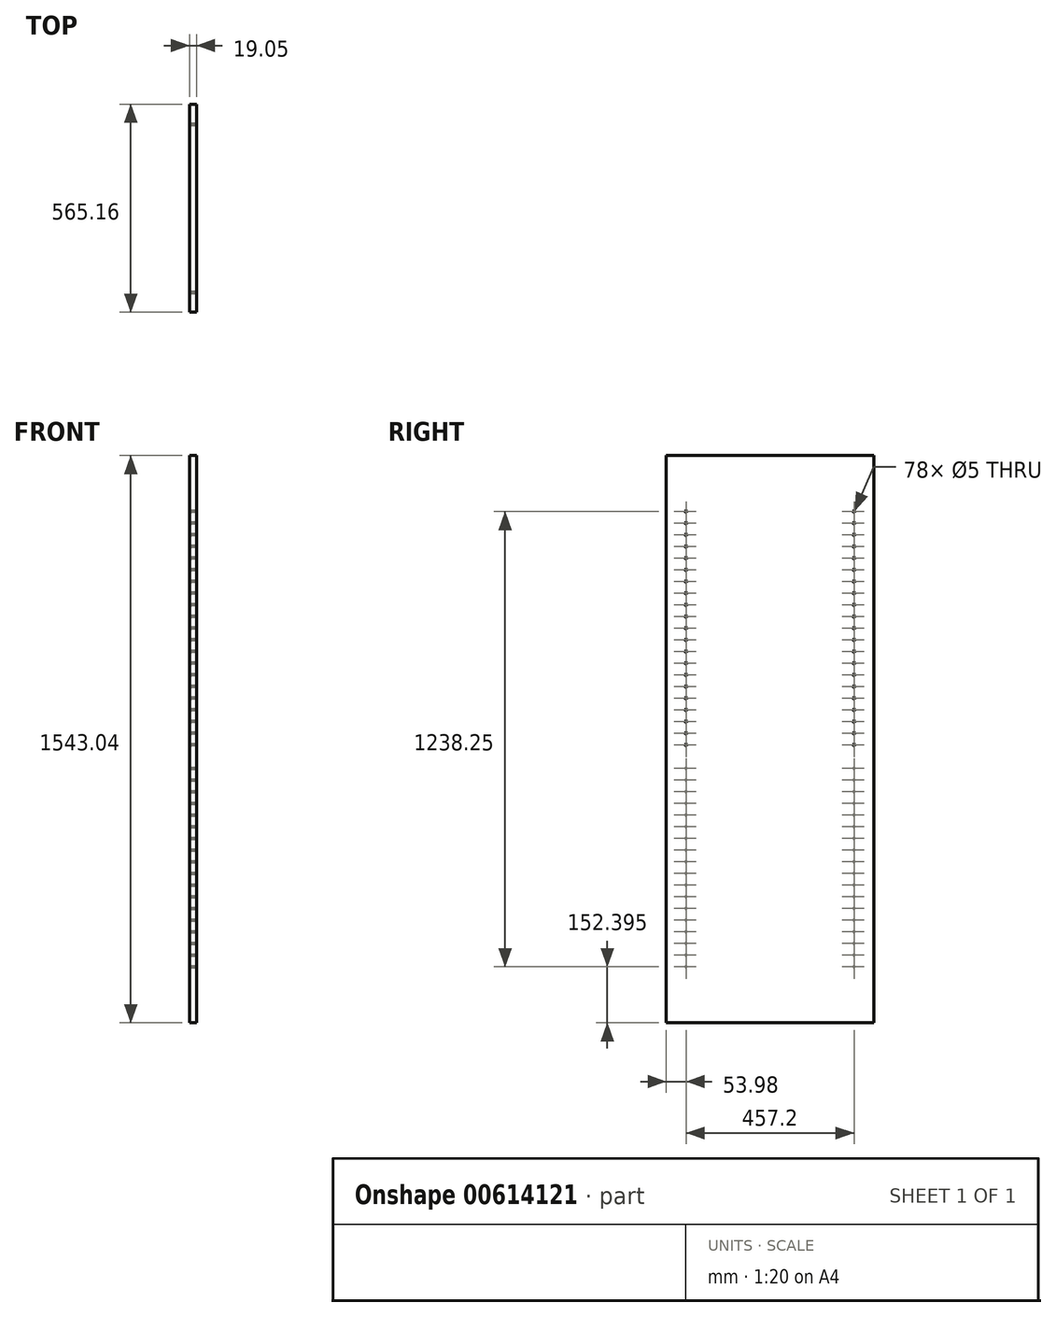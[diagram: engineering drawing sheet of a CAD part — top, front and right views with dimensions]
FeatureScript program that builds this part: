
annotation { "Feature Type Name" : "Feature", "Feature Type Description" : "" }
export const myFeature = defineFeature(function(context is Context, id is Id, definition is map)
    precondition{}
    {
        {
            var Q0;
            Q0=qCreatedBy(makeId("Right.planeOp"),FACE);
            var sketch = newSketch(context, id + "F0", { "sketchPlane" : qUnion([Q0])});
            skLineSegment(sketch, "E0.bottom", {"start": v(282.58, 771.53) * mm, "end": v(-282.57, 771.53) * mm});
            skLineSegment(sketch, "E0.top", {"start": v(282.57, -771.53) * mm, "end": v(-282.58, -771.53) * mm});
            skLineSegment(sketch, "E0.left", {"start": v(282.58, 771.53) * mm, "end": v(282.57, -771.53) * mm});
            skLineSegment(sketch, "E0.right", {"start": v(-282.57, 771.53) * mm, "end": v(-282.58, -771.53) * mm});
            skPoint(sketch, "E0.middle", {"position": v(0, 0) * mm});
            skSolve(sketch);
        }
        {
            var Q0;
            Q0=makeQuery(id+"F0.imprint","IMPRINT",FACE,{"disambiguationData":[TD([[makeQuery(id+"F0.imprint","IMPRINT",EDGE,{"derivedFrom":sQuery(id+"F0.wireOp",EDGE,"E0.bottom")}),1.0]])]});
            extrude(context, id + "F1", {"entities" : qUnion([Q0]), "depth" : 19.05 * mm, "offsetDistance" : 25.4 * mm});
        }
        {
            var Q0;
            Q0=makeQuery(id+"F1.opExtrude","CAP_FACE",FACE,{"disambiguationData":[OSD([sQuery(id+"F0.wireOp",EDGE,"E0.bottom"),sQuery(id+"F0.wireOp",EDGE,"E0.top"),sQuery(id+"F0.wireOp",EDGE,"E0.left"),sQuery(id+"F0.wireOp",EDGE,"E0.right")])],"isStart":false});
            var sketch = newSketch(context, id + "F2", { "sketchPlane" : qUnion([Q0])});
            skLineSegment(sketch, "E1", {"start": v(0, -771.53) * mm, "end": v(0, -9.53) * mm});
            skPoint(sketch, "E1.endSnap0", {"position": v(0, -771.53) * mm});
            skLineSegment(sketch, "E2", {"start": v(0, -9.53) * mm, "end": v(-282.58, -9.53) * mm});
            skLineSegment(sketch, "E3", {"start": v(0, 771.53) * mm, "end": v(0, 587.38) * mm});
            skPoint(sketch, "E3.endSnap0", {"position": v(0, 771.53) * mm});
            skLineSegment(sketch, "E4.bottom", {"start": v(228.6, 555.63) * mm, "end": v(-228.6, 555.63) * mm});
            skLineSegment(sketch, "E4.top", {"start": v(228.6, 619.13) * mm, "end": v(-228.6, 619.13) * mm});
            skLineSegment(sketch, "E4.left", {"start": v(228.6, 555.63) * mm, "end": v(228.6, 619.13) * mm});
            skLineSegment(sketch, "E4.right", {"start": v(-228.6, 555.63) * mm, "end": v(-228.6, 619.13) * mm});
            skPoint(sketch, "E4.middle", {"position": v(0, 587.38) * mm});
            skLineSegment(sketch, "E5", {"start": v(0, 555.63) * mm, "end": v(0, 492.13) * mm});
            skLineSegment(sketch, "E6.bottom", {"start": v(228.6, 523.88) * mm, "end": v(-228.6, 523.88) * mm});
            skLineSegment(sketch, "E6.top", {"start": v(228.6, 460.38) * mm, "end": v(-228.6, 460.38) * mm});
            skLineSegment(sketch, "E6.left", {"start": v(228.6, 523.88) * mm, "end": v(228.6, 460.38) * mm});
            skLineSegment(sketch, "E6.right", {"start": v(-228.6, 523.88) * mm, "end": v(-228.6, 460.38) * mm});
            skPoint(sketch, "E6.middle", {"position": v(0, 492.13) * mm});
            skLineSegment(sketch, "E7", {"start": v(0, 460.38) * mm, "end": v(0, 396.88) * mm});
            skLineSegment(sketch, "E8.bottom", {"start": v(228.6, 365.12) * mm, "end": v(-228.6, 365.12) * mm});
            skLineSegment(sketch, "E8.top", {"start": v(228.6, 428.62) * mm, "end": v(-228.6, 428.62) * mm});
            skLineSegment(sketch, "E8.left", {"start": v(228.6, 365.12) * mm, "end": v(228.6, 428.62) * mm});
            skLineSegment(sketch, "E8.right", {"start": v(-228.6, 365.12) * mm, "end": v(-228.6, 428.62) * mm});
            skPoint(sketch, "E8.middle", {"position": v(0, 396.88) * mm});
            skLineSegment(sketch, "E9", {"start": v(0, 365.12) * mm, "end": v(0, 301.62) * mm});
            skLineSegment(sketch, "E10.bottom", {"start": v(228.6, 333.38) * mm, "end": v(-228.6, 333.38) * mm});
            skLineSegment(sketch, "E10.top", {"start": v(228.6, 269.88) * mm, "end": v(-228.6, 269.87) * mm});
            skLineSegment(sketch, "E10.left", {"start": v(228.6, 333.38) * mm, "end": v(228.6, 269.88) * mm});
            skLineSegment(sketch, "E10.right", {"start": v(-228.6, 333.38) * mm, "end": v(-228.6, 269.88) * mm});
            skPoint(sketch, "E10.middle", {"position": v(0, 301.62) * mm});
            skLineSegment(sketch, "E11", {"start": v(0, 269.88) * mm, "end": v(0, 206.38) * mm});
            skLineSegment(sketch, "E12.bottom", {"start": v(228.6, 238.13) * mm, "end": v(-228.6, 238.13) * mm});
            skLineSegment(sketch, "E12.top", {"start": v(228.6, 174.63) * mm, "end": v(-228.6, 174.62) * mm});
            skLineSegment(sketch, "E12.left", {"start": v(228.6, 238.13) * mm, "end": v(228.6, 174.63) * mm});
            skLineSegment(sketch, "E12.right", {"start": v(-228.6, 238.13) * mm, "end": v(-228.6, 174.62) * mm});
            skPoint(sketch, "E12.middle", {"position": v(0, 206.38) * mm});
            skLineSegment(sketch, "E13", {"start": v(0, 174.63) * mm, "end": v(0, 111.13) * mm});
            skLineSegment(sketch, "E14.bottom", {"start": v(228.6, 79.37) * mm, "end": v(-228.6, 79.37) * mm});
            skLineSegment(sketch, "E14.top", {"start": v(228.6, 142.87) * mm, "end": v(-228.6, 142.87) * mm});
            skLineSegment(sketch, "E14.left", {"start": v(228.6, 79.37) * mm, "end": v(228.6, 142.87) * mm});
            skLineSegment(sketch, "E14.right", {"start": v(-228.6, 79.37) * mm, "end": v(-228.6, 142.87) * mm});
            skPoint(sketch, "E14.middle", {"position": v(0, 111.13) * mm});
            skLineSegment(sketch, "E15", {"start": v(0, 79.37) * mm, "end": v(0, 15.87) * mm});
            skLineSegment(sketch, "E16.bottom", {"start": v(228.6, 47.62) * mm, "end": v(-228.6, 47.62) * mm});
            skLineSegment(sketch, "E16.top", {"start": v(228.6, -15.88) * mm, "end": v(-228.6, -15.88) * mm});
            skLineSegment(sketch, "E16.left", {"start": v(228.6, 47.62) * mm, "end": v(228.6, -15.88) * mm});
            skLineSegment(sketch, "E16.right", {"start": v(-228.6, 47.62) * mm, "end": v(-228.6, -15.88) * mm});
            skPoint(sketch, "E16.middle", {"position": v(0, 15.87) * mm});
            skPoint(sketch, "E17", {"position": v(-228.6, 619.13) * mm});
            skPoint(sketch, "E18", {"position": v(-228.6, 587.38) * mm});
            skPoint(sketch, "E19", {"position": v(-228.6, 555.63) * mm});
            skPoint(sketch, "E20", {"position": v(-228.6, 523.88) * mm});
            skPoint(sketch, "E21", {"position": v(-228.6, 492.13) * mm});
            skPoint(sketch, "E22", {"position": v(-228.6, 460.38) * mm});
            skPoint(sketch, "E23", {"position": v(-228.6, 428.62) * mm});
            skPoint(sketch, "E24", {"position": v(-228.6, 396.87) * mm});
            skPoint(sketch, "E25", {"position": v(-228.6, 365.12) * mm});
            skPoint(sketch, "E26", {"position": v(-228.6, 333.38) * mm});
            skPoint(sketch, "E27", {"position": v(-228.6, 301.62) * mm});
            skPoint(sketch, "E28", {"position": v(-228.6, 269.88) * mm});
            skPoint(sketch, "E29", {"position": v(-228.6, 238.13) * mm});
            skPoint(sketch, "E30", {"position": v(-228.6, 206.38) * mm});
            skPoint(sketch, "E31", {"position": v(-228.6, 174.62) * mm});
            skPoint(sketch, "E32", {"position": v(-228.6, 142.87) * mm});
            skPoint(sketch, "E33", {"position": v(-228.6, 111.12) * mm});
            skPoint(sketch, "E34", {"position": v(-228.6, 79.37) * mm});
            skPoint(sketch, "E35", {"position": v(-228.6, 47.62) * mm});
            skPoint(sketch, "E36", {"position": v(-228.6, 15.87) * mm});
            skPoint(sketch, "E37", {"position": v(-228.6, -15.88) * mm});
            skPoint(sketch, "E38", {"position": v(228.6, -15.88) * mm});
            skPoint(sketch, "E39", {"position": v(228.6, 15.87) * mm});
            skPoint(sketch, "E40", {"position": v(228.6, 47.62) * mm});
            skPoint(sketch, "E41", {"position": v(228.6, 79.37) * mm});
            skPoint(sketch, "E42", {"position": v(228.6, 111.12) * mm});
            skPoint(sketch, "E43", {"position": v(228.6, 142.87) * mm});
            skPoint(sketch, "E44", {"position": v(228.6, 174.63) * mm});
            skPoint(sketch, "E45", {"position": v(228.6, 206.38) * mm});
            skPoint(sketch, "E46", {"position": v(228.6, 238.13) * mm});
            skPoint(sketch, "E47", {"position": v(228.6, 269.88) * mm});
            skPoint(sketch, "E48", {"position": v(228.6, 301.63) * mm});
            skPoint(sketch, "E49", {"position": v(228.6, 333.38) * mm});
            skPoint(sketch, "E50", {"position": v(228.6, 365.12) * mm});
            skPoint(sketch, "E51", {"position": v(228.6, 396.88) * mm});
            skPoint(sketch, "E52", {"position": v(228.6, 428.62) * mm});
            skPoint(sketch, "E53", {"position": v(228.6, 460.38) * mm});
            skPoint(sketch, "E54", {"position": v(228.6, 492.13) * mm});
            skPoint(sketch, "E55", {"position": v(228.6, 523.88) * mm});
            skPoint(sketch, "E56", {"position": v(228.6, 555.63) * mm});
            skPoint(sketch, "E57", {"position": v(228.6, 587.38) * mm});
            skPoint(sketch, "E58", {"position": v(228.6, 619.13) * mm});
            skSolve(sketch);
        }
        {
            var Q0;
            Q0=sQuery(id+"F2.wireOp",VERTEX,"E17");
            var Q1;
            Q1=sQuery(id+"F2.wireOp",VERTEX,"E18");
            var Q2;
            Q2=sQuery(id+"F2.wireOp",VERTEX,"E19");
            var Q3;
            Q3=sQuery(id+"F2.wireOp",VERTEX,"E20");
            var Q4;
            Q4=sQuery(id+"F2.wireOp",VERTEX,"E21");
            var Q5;
            Q5=sQuery(id+"F2.wireOp",VERTEX,"E22");
            var Q6;
            Q6=sQuery(id+"F2.wireOp",VERTEX,"E23");
            var Q7;
            Q7=sQuery(id+"F2.wireOp",VERTEX,"E24");
            var Q8;
            Q8=sQuery(id+"F2.wireOp",VERTEX,"E25");
            var Q9;
            Q9=sQuery(id+"F2.wireOp",VERTEX,"E26");
            var Q10;
            Q10=sQuery(id+"F2.wireOp",VERTEX,"E27");
            var Q11;
            Q11=sQuery(id+"F2.wireOp",VERTEX,"E28");
            var Q12;
            Q12=sQuery(id+"F2.wireOp",VERTEX,"E29");
            var Q13;
            Q13=sQuery(id+"F2.wireOp",VERTEX,"E30");
            var Q14;
            Q14=sQuery(id+"F2.wireOp",VERTEX,"E31");
            var Q15;
            Q15=sQuery(id+"F2.wireOp",VERTEX,"E32");
            var Q16;
            Q16=sQuery(id+"F2.wireOp",VERTEX,"E33");
            var Q17;
            Q17=sQuery(id+"F2.wireOp",VERTEX,"E34");
            var Q18;
            Q18=sQuery(id+"F2.wireOp",VERTEX,"E35");
            var Q19;
            Q19=sQuery(id+"F2.wireOp",VERTEX,"E36");
            var Q20;
            Q20=sQuery(id+"F2.wireOp",VERTEX,"E37");
            var Q21;
            Q21=sQuery(id+"F2.wireOp",VERTEX,"E58");
            var Q22;
            Q22=sQuery(id+"F2.wireOp",VERTEX,"E57");
            var Q23;
            Q23=sQuery(id+"F2.wireOp",VERTEX,"E56");
            var Q24;
            Q24=sQuery(id+"F2.wireOp",VERTEX,"E55");
            var Q25;
            Q25=sQuery(id+"F2.wireOp",VERTEX,"E54");
            var Q26;
            Q26=sQuery(id+"F2.wireOp",VERTEX,"E53");
            var Q27;
            Q27=sQuery(id+"F2.wireOp",VERTEX,"E52");
            var Q28;
            Q28=sQuery(id+"F2.wireOp",VERTEX,"E51");
            var Q29;
            Q29=sQuery(id+"F2.wireOp",VERTEX,"E50");
            var Q30;
            Q30=sQuery(id+"F2.wireOp",VERTEX,"E49");
            var Q31;
            Q31=sQuery(id+"F2.wireOp",VERTEX,"E48");
            var Q32;
            Q32=sQuery(id+"F2.wireOp",VERTEX,"E47");
            var Q33;
            Q33=sQuery(id+"F2.wireOp",VERTEX,"E46");
            var Q34;
            Q34=sQuery(id+"F2.wireOp",VERTEX,"E45");
            var Q35;
            Q35=sQuery(id+"F2.wireOp",VERTEX,"E44");
            var Q36;
            Q36=sQuery(id+"F2.wireOp",VERTEX,"E43");
            var Q37;
            Q37=sQuery(id+"F2.wireOp",VERTEX,"E42");
            var Q38;
            Q38=sQuery(id+"F2.wireOp",VERTEX,"E41");
            var Q39;
            Q39=sQuery(id+"F2.wireOp",VERTEX,"E40");
            var Q40;
            Q40=sQuery(id+"F2.wireOp",VERTEX,"E39");
            var Q41;
            Q41=sQuery(id+"F2.wireOp",VERTEX,"E38");
            var Q42;
            Q42=makeQuery(id+"F1.opExtrude","SWEPT_BODY",BODY,{"disambiguationData":[OSD([sQuery(id+"F0.wireOp",EDGE,"E0.bottom"),sQuery(id+"F0.wireOp",EDGE,"E0.top"),sQuery(id+"F0.wireOp",EDGE,"E0.left"),sQuery(id+"F0.wireOp",EDGE,"E0.right")])]});
            hole(context, id + "F3", {"style" : HoleStyle.SIMPLE, "endStyle" : HoleEndStyle.BLIND, "holeDiameter" : 5 * mm, "majorDiameter" : 6.35 * mm, "holeDepth" : 14.22 * mm, "isTappedThrough" : true, "tappedDepth" : 12.7 * mm, "tapClearance" : 3, "startFromSketch" : true, "locations" : qUnion([Q0, Q1, Q2, Q3, Q4, Q5, Q6, Q7, Q8, Q9, Q10, Q11, Q12, Q13, Q14, Q15, Q16, Q17, Q18, Q19, Q20, Q21, Q22, Q23, Q24, Q25, Q26, Q27, Q28, Q29, Q30, Q31, Q32, Q33, Q34, Q35, Q36, Q37, Q38, Q39, Q40, Q41]), "scope" : qUnion([Q42])});
        }
        {
            var Q0;
            Q0=makeQuery(id+"F1.opExtrude","CAP_FACE",FACE,{"disambiguationData":[OSD([sQuery(id+"F0.wireOp",EDGE,"E0.bottom"),sQuery(id+"F0.wireOp",EDGE,"E0.top"),sQuery(id+"F0.wireOp",EDGE,"E0.left"),sQuery(id+"F0.wireOp",EDGE,"E0.right")])],"isStart":true});
            var sketch = newSketch(context, id + "F4", { "sketchPlane" : qUnion([Q0])});
            skLineSegment(sketch, "E59", {"start": v(0, -771.53) * mm, "end": v(0, -587.38) * mm});
            skLineSegment(sketch, "E60.bottom", {"start": v(228.6, -555.62) * mm, "end": v(-228.6, -555.62) * mm});
            skLineSegment(sketch, "E60.top", {"start": v(228.6, -619.12) * mm, "end": v(-228.6, -619.12) * mm});
            skLineSegment(sketch, "E60.left", {"start": v(228.6, -555.62) * mm, "end": v(228.6, -619.12) * mm});
            skLineSegment(sketch, "E60.right", {"start": v(-228.6, -555.62) * mm, "end": v(-228.6, -619.12) * mm});
            skPoint(sketch, "E60.middle", {"position": v(0, -587.38) * mm});
            skLineSegment(sketch, "E61", {"start": v(0, -555.62) * mm, "end": v(0, -492.13) * mm});
            skPoint(sketch, "E61.endSnap0", {"position": v(0, -555.62) * mm});
            skLineSegment(sketch, "E62.bottom", {"start": v(228.6, -460.37) * mm, "end": v(-228.6, -460.37) * mm});
            skLineSegment(sketch, "E62.top", {"start": v(228.6, -523.87) * mm, "end": v(-228.6, -523.87) * mm});
            skLineSegment(sketch, "E62.left", {"start": v(228.6, -460.37) * mm, "end": v(228.6, -523.87) * mm});
            skLineSegment(sketch, "E62.right", {"start": v(-228.6, -460.37) * mm, "end": v(-228.6, -523.87) * mm});
            skPoint(sketch, "E62.middle", {"position": v(0, -492.13) * mm});
            skLineSegment(sketch, "E63", {"start": v(0, -460.37) * mm, "end": v(0, -396.87) * mm});
            skPoint(sketch, "E63.endSnap0", {"position": v(0, -460.37) * mm});
            skLineSegment(sketch, "E64.bottom", {"start": v(228.6, -365.12) * mm, "end": v(-228.6, -365.12) * mm});
            skLineSegment(sketch, "E64.top", {"start": v(228.6, -428.62) * mm, "end": v(-228.6, -428.62) * mm});
            skLineSegment(sketch, "E64.left", {"start": v(228.6, -365.12) * mm, "end": v(228.6, -428.62) * mm});
            skLineSegment(sketch, "E64.right", {"start": v(-228.6, -365.12) * mm, "end": v(-228.6, -428.62) * mm});
            skPoint(sketch, "E64.middle", {"position": v(0, -396.87) * mm});
            skLineSegment(sketch, "E65", {"start": v(0, -365.12) * mm, "end": v(0, -301.62) * mm});
            skPoint(sketch, "E65.endSnap0", {"position": v(0, -365.12) * mm});
            skLineSegment(sketch, "E66.bottom", {"start": v(228.6, -269.87) * mm, "end": v(-228.6, -269.87) * mm});
            skLineSegment(sketch, "E66.top", {"start": v(228.6, -333.37) * mm, "end": v(-228.6, -333.37) * mm});
            skLineSegment(sketch, "E66.left", {"start": v(228.6, -269.87) * mm, "end": v(228.6, -333.37) * mm});
            skLineSegment(sketch, "E66.right", {"start": v(-228.6, -269.87) * mm, "end": v(-228.6, -333.37) * mm});
            skPoint(sketch, "E66.middle", {"position": v(0, -301.62) * mm});
            skLineSegment(sketch, "E67", {"start": v(0, -269.87) * mm, "end": v(0, -206.37) * mm});
            skPoint(sketch, "E67.endSnap0", {"position": v(0, -269.87) * mm});
            skLineSegment(sketch, "E68.bottom", {"start": v(228.6, -238.12) * mm, "end": v(-228.6, -238.12) * mm});
            skLineSegment(sketch, "E68.top", {"start": v(228.6, -174.62) * mm, "end": v(-228.6, -174.62) * mm});
            skLineSegment(sketch, "E68.left", {"start": v(228.6, -238.12) * mm, "end": v(228.6, -174.62) * mm});
            skLineSegment(sketch, "E68.right", {"start": v(-228.6, -238.12) * mm, "end": v(-228.6, -174.62) * mm});
            skPoint(sketch, "E68.middle", {"position": v(0, -206.37) * mm});
            skLineSegment(sketch, "E69", {"start": v(0, -174.62) * mm, "end": v(0, -111.12) * mm});
            skLineSegment(sketch, "E70.bottom", {"start": v(228.6, -79.37) * mm, "end": v(-228.6, -79.37) * mm});
            skLineSegment(sketch, "E70.top", {"start": v(228.6, -142.87) * mm, "end": v(-228.6, -142.87) * mm});
            skLineSegment(sketch, "E70.left", {"start": v(228.6, -79.37) * mm, "end": v(228.6, -142.87) * mm});
            skLineSegment(sketch, "E70.right", {"start": v(-228.6, -79.37) * mm, "end": v(-228.6, -142.87) * mm});
            skPoint(sketch, "E70.middle", {"position": v(0, -111.12) * mm});
            skPoint(sketch, "E71", {"position": v(-228.6, -79.37) * mm});
            skPoint(sketch, "E72", {"position": v(-228.6, -111.12) * mm});
            skPoint(sketch, "E73", {"position": v(-228.6, -142.87) * mm});
            skPoint(sketch, "E74", {"position": v(-228.6, -174.62) * mm});
            skPoint(sketch, "E75", {"position": v(-228.6, -206.37) * mm});
            skPoint(sketch, "E76", {"position": v(-228.6, -238.12) * mm});
            skPoint(sketch, "E77", {"position": v(-228.6, -269.87) * mm});
            skPoint(sketch, "E78", {"position": v(-228.6, -301.62) * mm});
            skPoint(sketch, "E79", {"position": v(-228.6, -333.37) * mm});
            skPoint(sketch, "E80", {"position": v(-228.6, -365.12) * mm});
            skPoint(sketch, "E81", {"position": v(-228.6, -396.87) * mm});
            skPoint(sketch, "E82", {"position": v(-228.6, -428.62) * mm});
            skPoint(sketch, "E83", {"position": v(-228.6, -460.37) * mm});
            skPoint(sketch, "E84", {"position": v(-228.6, -492.12) * mm});
            skPoint(sketch, "E85", {"position": v(-228.6, -523.87) * mm});
            skPoint(sketch, "E86", {"position": v(-228.6, -555.62) * mm});
            skPoint(sketch, "E87", {"position": v(-228.6, -587.38) * mm});
            skPoint(sketch, "E88", {"position": v(-228.6, -619.12) * mm});
            skPoint(sketch, "E89", {"position": v(228.6, -619.12) * mm});
            skPoint(sketch, "E90", {"position": v(228.6, -587.38) * mm});
            skPoint(sketch, "E91", {"position": v(228.6, -555.62) * mm});
            skPoint(sketch, "E92", {"position": v(228.6, -523.87) * mm});
            skPoint(sketch, "E93", {"position": v(228.6, -492.12) * mm});
            skPoint(sketch, "E94", {"position": v(228.6, -460.37) * mm});
            skPoint(sketch, "E95", {"position": v(228.6, -428.62) * mm});
            skPoint(sketch, "E96", {"position": v(228.6, -396.87) * mm});
            skPoint(sketch, "E97", {"position": v(228.6, -365.12) * mm});
            skPoint(sketch, "E98", {"position": v(228.6, -333.37) * mm});
            skPoint(sketch, "E99", {"position": v(228.6, -301.62) * mm});
            skPoint(sketch, "E100", {"position": v(228.6, -269.87) * mm});
            skPoint(sketch, "E101", {"position": v(228.6, -238.12) * mm});
            skPoint(sketch, "E102", {"position": v(228.6, -206.37) * mm});
            skPoint(sketch, "E103", {"position": v(228.6, -174.62) * mm});
            skPoint(sketch, "E104", {"position": v(228.6, -142.87) * mm});
            skPoint(sketch, "E105", {"position": v(228.6, -111.12) * mm});
            skPoint(sketch, "E106", {"position": v(228.6, -79.37) * mm});
            skSolve(sketch);
        }
        {
            var Q0;
            Q0=sQuery(id+"F4.wireOp",VERTEX,"E71");
            var Q1;
            Q1=sQuery(id+"F4.wireOp",VERTEX,"E72");
            var Q2;
            Q2=sQuery(id+"F4.wireOp",VERTEX,"E73");
            var Q3;
            Q3=sQuery(id+"F4.wireOp",VERTEX,"E74");
            var Q4;
            Q4=sQuery(id+"F4.wireOp",VERTEX,"E75");
            var Q5;
            Q5=sQuery(id+"F4.wireOp",VERTEX,"E76");
            var Q6;
            Q6=sQuery(id+"F4.wireOp",VERTEX,"E77");
            var Q7;
            Q7=sQuery(id+"F4.wireOp",VERTEX,"E78");
            var Q8;
            Q8=sQuery(id+"F4.wireOp",VERTEX,"E79");
            var Q9;
            Q9=sQuery(id+"F4.wireOp",VERTEX,"E80");
            var Q10;
            Q10=sQuery(id+"F4.wireOp",VERTEX,"E81");
            var Q11;
            Q11=sQuery(id+"F4.wireOp",VERTEX,"E82");
            var Q12;
            Q12=sQuery(id+"F4.wireOp",VERTEX,"E83");
            var Q13;
            Q13=sQuery(id+"F4.wireOp",VERTEX,"E85");
            var Q14;
            Q14=sQuery(id+"F4.wireOp",VERTEX,"E84");
            var Q15;
            Q15=sQuery(id+"F4.wireOp",VERTEX,"E86");
            var Q16;
            Q16=sQuery(id+"F4.wireOp",VERTEX,"E87");
            var Q17;
            Q17=sQuery(id+"F4.wireOp",VERTEX,"E88");
            var Q18;
            Q18=sQuery(id+"F4.wireOp",VERTEX,"E89");
            var Q19;
            Q19=sQuery(id+"F4.wireOp",VERTEX,"E90");
            var Q20;
            Q20=sQuery(id+"F4.wireOp",VERTEX,"E91");
            var Q21;
            Q21=sQuery(id+"F4.wireOp",VERTEX,"E92");
            var Q22;
            Q22=sQuery(id+"F4.wireOp",VERTEX,"E93");
            var Q23;
            Q23=sQuery(id+"F4.wireOp",VERTEX,"E94");
            var Q24;
            Q24=sQuery(id+"F4.wireOp",VERTEX,"E95");
            var Q25;
            Q25=sQuery(id+"F4.wireOp",VERTEX,"E96");
            var Q26;
            Q26=sQuery(id+"F4.wireOp",VERTEX,"E97");
            var Q27;
            Q27=sQuery(id+"F4.wireOp",VERTEX,"E98");
            var Q28;
            Q28=sQuery(id+"F4.wireOp",VERTEX,"E99");
            var Q29;
            Q29=sQuery(id+"F4.wireOp",VERTEX,"E100");
            var Q30;
            Q30=sQuery(id+"F4.wireOp",VERTEX,"E101");
            var Q31;
            Q31=sQuery(id+"F4.wireOp",VERTEX,"E103");
            var Q32;
            Q32=sQuery(id+"F4.wireOp",VERTEX,"E102");
            var Q33;
            Q33=sQuery(id+"F4.wireOp",VERTEX,"E104");
            var Q34;
            Q34=sQuery(id+"F4.wireOp",VERTEX,"E105");
            var Q35;
            Q35=sQuery(id+"F4.wireOp",VERTEX,"E106");
            var Q36;
            Q36=makeQuery(id+"F1.opExtrude","SWEPT_BODY",BODY,{"disambiguationData":[OSD([sQuery(id+"F0.wireOp",EDGE,"E0.bottom"),sQuery(id+"F0.wireOp",EDGE,"E0.top"),sQuery(id+"F0.wireOp",EDGE,"E0.left"),sQuery(id+"F0.wireOp",EDGE,"E0.right")])]});
            hole(context, id + "F5", {"style" : HoleStyle.SIMPLE, "endStyle" : HoleEndStyle.BLIND, "holeDiameter" : 5 * mm, "majorDiameter" : 6.35 * mm, "holeDepth" : 14.22 * mm, "isTappedThrough" : true, "tappedDepth" : 12.7 * mm, "tapClearance" : 3, "startFromSketch" : true, "locations" : qUnion([Q0, Q1, Q2, Q3, Q4, Q5, Q6, Q7, Q8, Q9, Q10, Q11, Q12, Q13, Q14, Q15, Q16, Q17, Q18, Q19, Q20, Q21, Q22, Q23, Q24, Q25, Q26, Q27, Q28, Q29, Q30, Q31, Q32, Q33, Q34, Q35]), "scope" : qUnion([Q36])});
        }
    });
